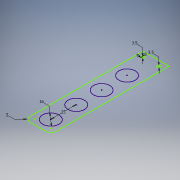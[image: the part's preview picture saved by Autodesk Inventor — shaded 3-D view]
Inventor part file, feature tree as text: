
AUTODESK INVENTOR PART (.ipt)
format: ipt  version: 2018.3 (Build 223284000, 284)  size: 95,232 bytes
history: native  units: in
note: dims shown in document units (in); Inventor stores cm internally (conversion verified against a paired STEP export)
features: sketch x1
ambient origin geometry x8: Origin, YZ Plane, XZ Plane, XY Plane, X Axis, Y Axis, Z Axis, Center Point
feature tree (1):
  sketch  "Sketch1"  dims[d0=0.6299in d1=1.5748in d3=0.9843in d4=0.3937in d6=0.3937in d9=0.1378in d10=0.1969in d11=0.1969in d13=1.5748in d15=0.3937in d16=0.1378in d17=0.1969in]
